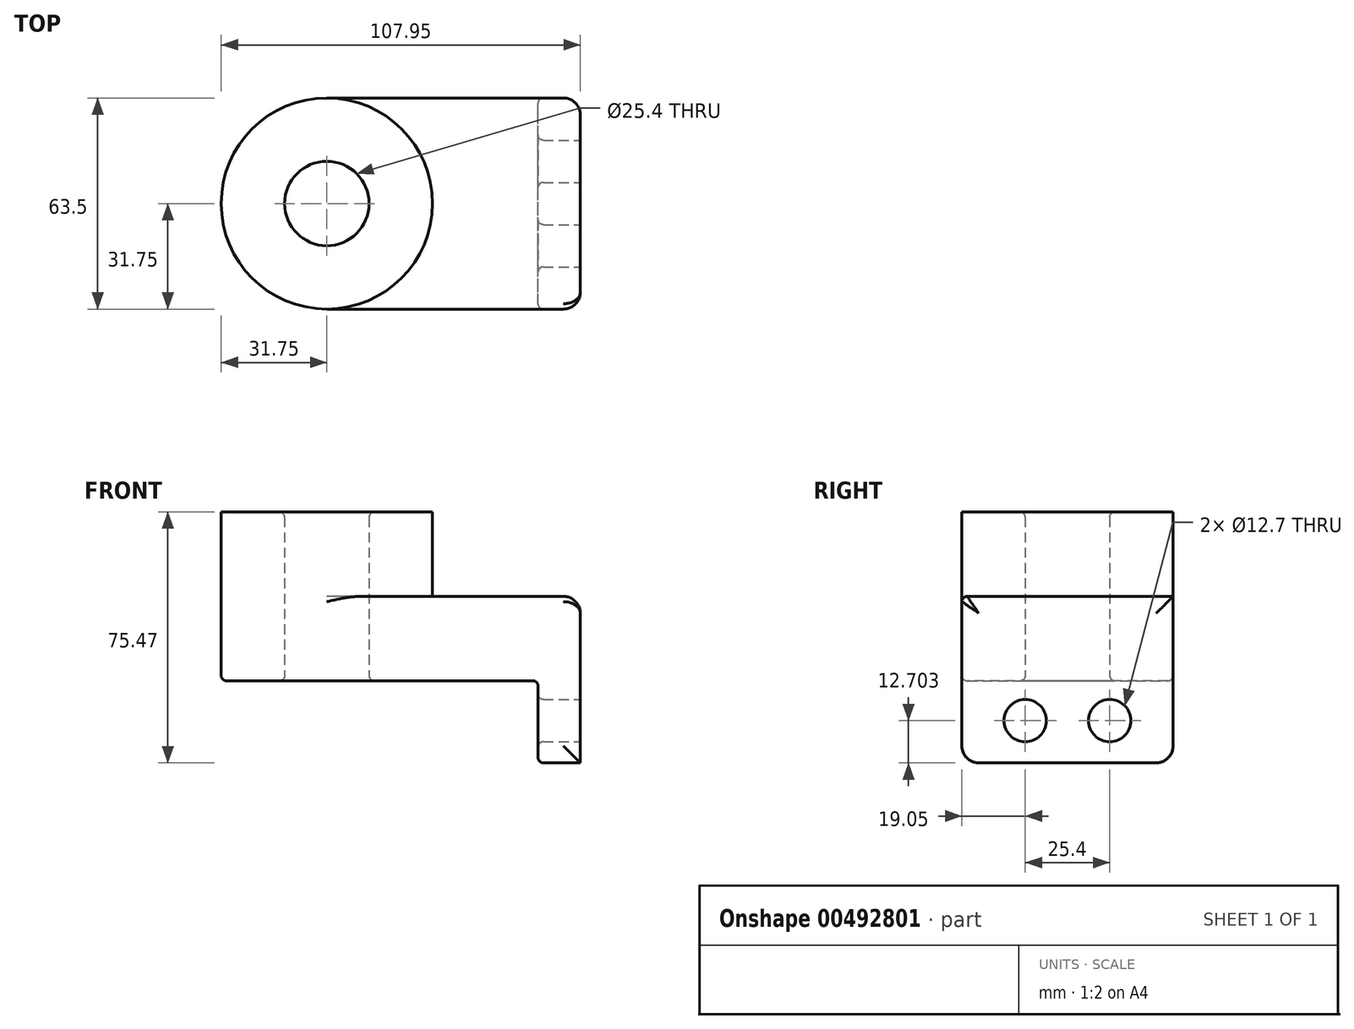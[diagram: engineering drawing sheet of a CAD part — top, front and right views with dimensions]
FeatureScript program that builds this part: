
annotation { "Feature Type Name" : "Feature", "Feature Type Description" : "" }
export const myFeature = defineFeature(function(context is Context, id is Id, definition is map)
    precondition{}
    {
        {
            var Q0;
            Q0=qCreatedBy(makeId("Top.planeOp"),FACE);
            var sketch = newSketch(context, id + "F0", { "sketchPlane" : qUnion([Q0])});
            skLineSegment(sketch, "E0.bottom", {"start": v(38.1, -31.75) * mm, "end": v(-38.1, -31.75) * mm});
            skLineSegment(sketch, "E0.top", {"start": v(38.1, 31.75) * mm, "end": v(-38.1, 31.75) * mm});
            skLineSegment(sketch, "E0.left", {"start": v(38.1, -31.75) * mm, "end": v(38.1, 31.75) * mm});
            skLineSegment(sketch, "E0.right", {"start": v(-38.1, -31.75) * mm, "end": v(-38.1, 31.75) * mm});
            skPoint(sketch, "E0.middle", {"position": v(0, 0) * mm});
            skCircle(sketch, "E1", {"center": v(-38.1, 0) * mm, "radius": 31.75 * mm});
            skCircle(sketch, "E2", {"center": v(-38.1, 0) * mm, "radius": 12.7 * mm});
            skSolve(sketch);
        }
        {
            var Q0;
            {var subQ1=sQuery(id+"F0.wireOp",EDGE,"E0.right");var subQ3=sQuery(id+"F0.wireOp",EDGE,"E2");var subQ4=makeQuery(id+"F0.imprint","INTERSECT",VERTEX,{"disambiguationData":[OD(0.0)],"derivedFrom":[subQ1,subQ3]});Q0=makeQuery(id+"F0.imprint","IMPRINT",FACE,{"disambiguationData":[TD([[makeQuery(id+"F0.imprint","IMPRINT",EDGE,{"disambiguationData":[TD([[subQ4,1.0]])],"derivedFrom":subQ3}),-1.0]])]});}
            var Q1;
            {var subQ1=sQuery(id+"F0.wireOp",EDGE,"E0.right");var subQ3=sQuery(id+"F0.wireOp",EDGE,"E2");var subQ4=makeQuery(id+"F0.imprint","INTERSECT",VERTEX,{"disambiguationData":[OD(0.0)],"derivedFrom":[subQ1,subQ3]});Q1=makeQuery(id+"F0.imprint","IMPRINT",FACE,{"disambiguationData":[TD([[makeQuery(id+"F0.imprint","IMPRINT",EDGE,{"disambiguationData":[TD([[subQ4,-1.0]])],"derivedFrom":subQ3}),-1.0]])]});}
            extrude(context, id + "F1", {"entities" : qUnion([Q0, Q1]), "depth" : 50.8 * mm});
        }
        {
            var Q0;
            {var subQ0=sQuery(id+"F0.wireOp",EDGE,"E0.bottom");Q0=makeQuery(id+"F0.imprint","IMPRINT",FACE,{"disambiguationData":[TD([[makeQuery(id+"F0.imprint","IMPRINT",EDGE,{"derivedFrom":subQ0}),-1.0]])]});}
            extrude(context, id + "F2", {"entities" : qUnion([Q0]), "operationType" : NewBodyOperationType.ADD, "depth" : 25.4 * mm});
        }
        {
            var Q0;
            Q0=makeQuery(id+"F2.opExtrude","SWEPT_FACE",FACE,{"disambiguationData":[OSD([sQuery(id+"F0.wireOp",EDGE,"E0.left")])]});
            var sketch = newSketch(context, id + "F3", { "sketchPlane" : qUnion([Q0])});
            skLineSegment(sketch, "E3.bottom", {"start": v(-31.75, 25.4) * mm, "end": v(31.75, 25.4) * mm});
            skLineSegment(sketch, "E3.top", {"start": v(-31.75, -24.67) * mm, "end": v(31.75, -24.67) * mm});
            skLineSegment(sketch, "E3.left", {"start": v(-31.75, 25.4) * mm, "end": v(-31.75, -24.67) * mm});
            skLineSegment(sketch, "E3.right", {"start": v(31.75, 25.4) * mm, "end": v(31.75, -24.67) * mm});
            skCircle(sketch, "E4", {"center": v(-12.7, -11.97) * mm, "radius": 6.35 * mm});
            skLineSegment(sketch, "E5", {"start": v(0, 0) * mm, "end": v(0, -24.67) * mm, "construction": true});
            skCircle(sketch, "E6.MirrorC", {"center": v(12.7, -11.97) * mm, "radius": 6.35 * mm});
            skSolve(sketch);
        }
        {
            var Q0;
            Q0 = qSketchRegion(id + "F3", true);
            extrude(context, id + "F4", {"entities" : qUnion([Q0]), "operationType" : NewBodyOperationType.ADD, "oppositeDirection" : true, "depth" : 12.7 * mm});
        }
        {
            var Q0;
            Q0=makeQuery(id+"F2.opExtrude","CAP_EDGE",EDGE,{"disambiguationData":[OSD([sQuery(id+"F0.wireOp",EDGE,"E1")])],"isStart":false});
            var Q1;
            Q1=makeQuery(id+"F2.opExtrude","CAP_EDGE",EDGE,{"disambiguationData":[OSD([sQuery(id+"F0.wireOp",EDGE,"E0.left")])],"isStart":false});
            var Q2;
            Q2=makeQuery(id+"F4.opExtrude","SWEPT_EDGE",EDGE,{"disambiguationData":[OSD([sQuery(id+"F3.wireOp",EDGE,"E3.top"),sQuery(id+"F3.wireOp",EDGE,"E3.left")])]});
            var Q3;
            Q3=makeQuery(id+"F4.boolean.opBoolean","MERGE",EDGE,{"derivedFrom":[makeQuery(id+"F2.opExtrude","SWEPT_EDGE",EDGE,{"disambiguationData":[OSD([sQuery(id+"F0.wireOp",EDGE,"E0.bottom"),sQuery(id+"F0.wireOp",EDGE,"E0.left")])]}),makeQuery(id+"F4.opExtrude","CAP_EDGE",EDGE,{"disambiguationData":[OSD([sQuery(id+"F3.wireOp",EDGE,"E3.left")])],"isStart":true})]});
            var Q4;
            Q4=makeQuery(id+"F4.boolean.opBoolean","MERGE",EDGE,{"derivedFrom":[makeQuery(id+"F2.opExtrude","SWEPT_EDGE",EDGE,{"disambiguationData":[OSD([sQuery(id+"F0.wireOp",EDGE,"E0.top"),sQuery(id+"F0.wireOp",EDGE,"E0.left")])]}),makeQuery(id+"F4.opExtrude","CAP_EDGE",EDGE,{"disambiguationData":[OSD([sQuery(id+"F3.wireOp",EDGE,"E3.right")])],"isStart":true})]});
            var Q5;
            Q5=makeQuery(id+"F4.opExtrude","SWEPT_EDGE",EDGE,{"disambiguationData":[OSD([sQuery(id+"F3.wireOp",EDGE,"E3.top"),sQuery(id+"F3.wireOp",EDGE,"E3.right")])]});
            fillet(context, id + "F5", {"entities" : qUnion([Q0, Q1, Q2, Q3, Q4, Q5]), "radius" : 5.08 * mm, "tangentPropagation" : true, "allowEdgeOverflow" : false});
        }
        {
            var Q0;
            Q0=makeQuery(id+"F2.opExtrude","CAP_EDGE",EDGE,{"disambiguationData":[OSD([sQuery(id+"F0.wireOp",EDGE,"E0.bottom")])],"isStart":false});
            var Q1;
            Q1=makeQuery(id+"F2.opExtrude","CAP_EDGE",EDGE,{"disambiguationData":[OSD([sQuery(id+"F0.wireOp",EDGE,"E0.bottom")])],"isStart":true});
            var Q2;
            Q2=makeQuery(id+"F4.opExtrude","CAP_FACE",FACE,{"disambiguationData":[OSD([sQuery(id+"F3.wireOp",EDGE,"E3.bottom"),sQuery(id+"F3.wireOp",EDGE,"E3.top"),sQuery(id+"F3.wireOp",EDGE,"E3.left"),sQuery(id+"F3.wireOp",EDGE,"E3.right"),sQuery(id+"F3.wireOp",EDGE,"E4"),sQuery(id+"F3.wireOp",EDGE,"E6.MirrorC")])],"isStart":false});
            var Q3;
            Q3=makeQuery(id+"F1.opExtrude","SWEPT_FACE",FACE,{"disambiguationData":[OSD([sQuery(id+"F0.wireOp",EDGE,"E2")])]});
            fillet(context, id + "F6", {"entities" : qUnion([Q0, Q1, Q2, Q3]), "radius" : 1.59 * mm, "tangentPropagation" : true, "allowEdgeOverflow" : false});
        }
    });
